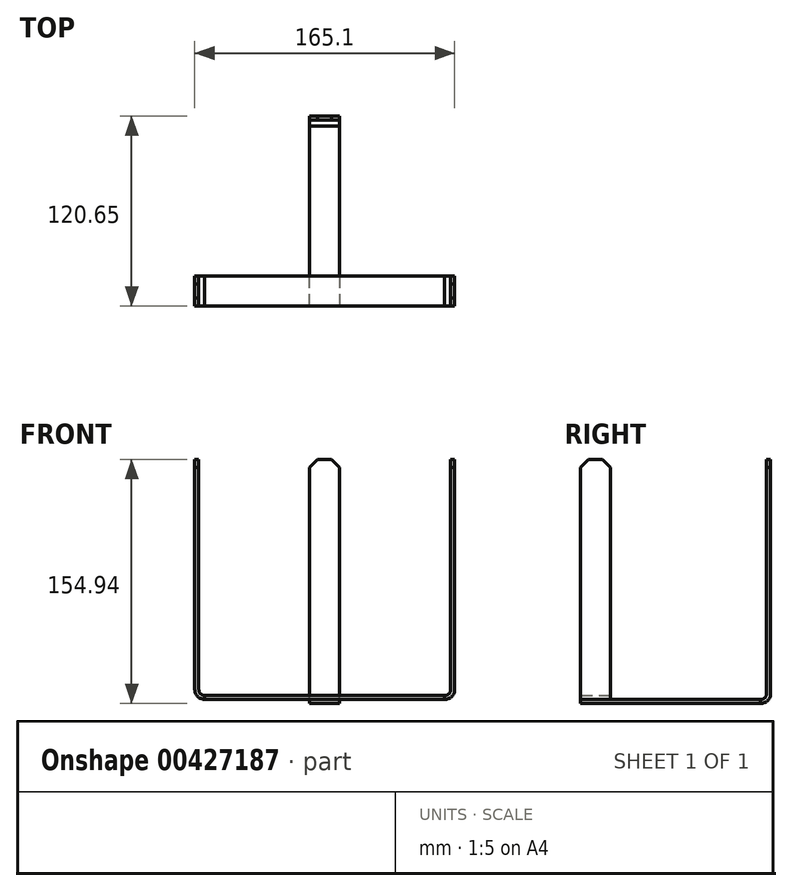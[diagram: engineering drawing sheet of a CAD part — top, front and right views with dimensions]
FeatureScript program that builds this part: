
annotation { "Feature Type Name" : "Feature", "Feature Type Description" : "" }
export const myFeature = defineFeature(function(context is Context, id is Id, definition is map)
    precondition{}
    {
        {
            var Q0;
            Q0=qCreatedBy(makeId("Top.planeOp"),FACE);
            var sketch = newSketch(context, id + "F0", { "sketchPlane" : qUnion([Q0])});
            skLineSegment(sketch, "E0.bottom", {"start": v(76.2, 9.53) * mm, "end": v(-76.2, 9.53) * mm});
            skLineSegment(sketch, "E0.top", {"start": v(76.2, -9.53) * mm, "end": v(-76.2, -9.53) * mm});
            skLineSegment(sketch, "E0.left", {"start": v(76.2, 9.53) * mm, "end": v(76.2, -9.53) * mm});
            skLineSegment(sketch, "E0.right", {"start": v(-76.2, 9.53) * mm, "end": v(-76.2, -9.53) * mm});
            skPoint(sketch, "E0.middle", {"position": v(0, 0) * mm});
            skLineSegment(sketch, "E1", {"start": v(0, 0) * mm, "end": v(-9.53, 0) * mm});
            skLineSegment(sketch, "E2", {"start": v(-9.53, -9.53) * mm, "end": v(-9.53, 104.78) * mm});
            skLineSegment(sketch, "E3", {"start": v(-9.53, 104.78) * mm, "end": v(9.52, 104.78) * mm});
            skLineSegment(sketch, "E4", {"start": v(9.52, 104.78) * mm, "end": v(9.53, -9.53) * mm});
            skSolve(sketch);
        }
        {
            var Q0;
            Q0=qCreatedBy(makeId("Front.planeOp"),FACE);
            var sketch = newSketch(context, id + "F1", { "sketchPlane" : qUnion([Q0])});
            skLineSegment(sketch, "E5", {"start": v(0, 0) * mm, "end": v(76.2, 0) * mm});
            skLineSegment(sketch, "E6", {"start": v(0, 0) * mm, "end": v(-76.2, 0) * mm});
            skArc(sketch, "E7", {"start": v(76.2, 0) * mm, "mid": v(80.7, 1.86) * mm, "end": v(82.55, 6.35) * mm});
            skArc(sketch, "E8", {"start": v(-82.55, 6.35) * mm, "mid": v(-80.7, 1.86) * mm, "end": v(-76.2, 0) * mm});
            skLineSegment(sketch, "E9", {"start": v(82.55, 0) * mm, "end": v(101.39, 0) * mm});
            skLineSegment(sketch, "E10", {"start": v(-82.55, 0) * mm, "end": v(-98.59, 0) * mm});
            skLineSegment(sketch, "E11", {"start": v(-82.55, 6.35) * mm, "end": v(-82.55, 21.04) * mm});
            skLineSegment(sketch, "E12", {"start": v(82.55, 6.35) * mm, "end": v(82.55, 20.48) * mm});
            skLineSegment(sketch, "E13", {"start": v(82.55, 6.35) * mm, "end": v(82.55, 152.4) * mm});
            skLineSegment(sketch, "E14", {"start": v(-82.55, 6.35) * mm, "end": v(-82.55, 152.4) * mm});
            skSolve(sketch);
        }
        {
            var Q0;
            Q0=qCreatedBy(makeId("Right.planeOp"),FACE);
            cPlane(context, id + "F2", {"entities" : qUnion([Q0]), "cplaneType" : CPlaneType.OFFSET, "offset" : 76.2 * mm, "width" : 152.4 * mm, "height" : 152.4 * mm});
        }
        {
            var Q0;
            Q0=qCreatedBy(id+"F2.planeOp",FACE);
            var sketch = newSketch(context, id + "F3", { "sketchPlane" : qUnion([Q0])});
            skLineSegment(sketch, "E15", {"start": v(0, 0) * mm, "end": v(-9.53, 0) * mm});
            skLineSegment(sketch, "E16", {"start": v(0, 0) * mm, "end": v(9.53, 0) * mm});
            skLineSegment(sketch, "E17", {"start": v(-9.53, 0) * mm, "end": v(-9.53, 2.54) * mm});
            skLineSegment(sketch, "E18", {"start": v(-9.53, 2.54) * mm, "end": v(9.53, 2.54) * mm});
            skLineSegment(sketch, "E19", {"start": v(9.53, 2.54) * mm, "end": v(9.53, 0) * mm});
            skSolve(sketch);
        }
        {
            var Q0;
            Q0=makeQuery(id+"F3.imprint","IMPRINT",FACE,{"disambiguationData":[TD([[makeQuery(id+"F3.imprint","IMPRINT",EDGE,{"derivedFrom":sQuery(id+"F3.wireOp",EDGE,"E15")}),-1.0]])]});
            var Q1;
            Q1=sQuery(id+"F1.wireOp",EDGE,"E13");
            var Q2;
            Q2=sQuery(id+"F1.wireOp",EDGE,"E7");
            sweep(context, id + "F4", {"profiles" : qUnion([Q0]), "path" : qUnion([Q1, Q2])});
        }
        {
            var Q0;
            Q0=qCreatedBy(makeId("Right.planeOp"),FACE);
            cPlane(context, id + "F5", {"entities" : qUnion([Q0]), "cplaneType" : CPlaneType.OFFSET, "offset" : 76.2 * mm, "oppositeDirection" : true, "width" : 152.4 * mm, "height" : 152.4 * mm});
        }
        {
            var Q0;
            Q0=qCreatedBy(id+"F5.planeOp",FACE);
            var sketch = newSketch(context, id + "F6", { "sketchPlane" : qUnion([Q0])});
            skLineSegment(sketch, "E20", {"start": v(0, 0) * mm, "end": v(-9.53, 0) * mm});
            skLineSegment(sketch, "E21", {"start": v(-9.53, 0) * mm, "end": v(-9.53, 2.54) * mm});
            skLineSegment(sketch, "E22", {"start": v(-9.53, 2.54) * mm, "end": v(9.53, 2.54) * mm});
            skLineSegment(sketch, "E23", {"start": v(9.53, 2.54) * mm, "end": v(9.53, 0) * mm});
            skLineSegment(sketch, "E24", {"start": v(9.53, 0) * mm, "end": v(0, 0) * mm});
            skSolve(sketch);
        }
        {
            var Q0;
            Q0=makeQuery(id+"F6.imprint","IMPRINT",FACE,{"disambiguationData":[TD([[makeQuery(id+"F6.imprint","IMPRINT",EDGE,{"derivedFrom":sQuery(id+"F6.wireOp",EDGE,"E20")}),-1.0]])]});
            var Q1;
            Q1=sQuery(id+"F1.wireOp",EDGE,"E8");
            var Q2;
            Q2=sQuery(id+"F1.wireOp",EDGE,"E14");
            sweep(context, id + "F7", {"profiles" : qUnion([Q0]), "path" : qUnion([Q1, Q2])});
        }
        {
            var Q0;
            {var subQ4=sQuery(id+"F0.wireOp",EDGE,"E0.right");Q0=makeQuery(id+"F0.imprint","IMPRINT",FACE,{"disambiguationData":[TD([[makeQuery(id+"F0.imprint","IMPRINT",EDGE,{"derivedFrom":subQ4}),1.0]])]});}
            var Q1;
            {var subQ0=sQuery(id+"F0.wireOp",EDGE,"E2");var subQ1=makeQuery(id+"F0.imprint","IMPRINT",VERTEX,{"derivedFrom":subQ0});Q1=makeQuery(id+"F0.imprint","IMPRINT",FACE,{"disambiguationData":[TD([[makeQuery(id+"F0.imprint","IMPRINT",EDGE,{"disambiguationData":[TD([[subQ1,1.0]])],"derivedFrom":subQ0}),-1.0]])]});}
            var Q2;
            {var subQ0=sQuery(id+"F0.wireOp",EDGE,"E0.left");Q2=makeQuery(id+"F0.imprint","IMPRINT",FACE,{"disambiguationData":[TD([[makeQuery(id+"F0.imprint","IMPRINT",EDGE,{"derivedFrom":subQ0}),-1.0]])]});}
            extrude(context, id + "F8", {"entities" : qUnion([Q0, Q1, Q2]), "depth" : 2.54 * mm});
        }
        {
            var Q0;
            Q0=qCreatedBy(makeId("Front.planeOp"),FACE);
            cPlane(context, id + "F9", {"entities" : qUnion([Q0]), "cplaneType" : CPlaneType.OFFSET, "offset" : 104.77 * mm, "oppositeDirection" : true, "width" : 152.4 * mm, "height" : 152.4 * mm});
        }
        {
            var Q0;
            Q0=qCreatedBy(id+"F9.planeOp",FACE);
            var sketch = newSketch(context, id + "F10", { "sketchPlane" : qUnion([Q0])});
            skLineSegment(sketch, "E25", {"start": v(0, 0) * mm, "end": v(9.53, 0) * mm});
            skLineSegment(sketch, "E26", {"start": v(9.53, 0) * mm, "end": v(9.53, 3.73) * mm});
            skLineSegment(sketch, "E27", {"start": v(9.53, 3.73) * mm, "end": v(-9.53, 3.73) * mm});
            skLineSegment(sketch, "E28", {"start": v(-9.53, 3.73) * mm, "end": v(-9.53, 0) * mm});
            skLineSegment(sketch, "E29", {"start": v(-9.53, 0) * mm, "end": v(0, 0) * mm});
            skLineSegment(sketch, "E30", {"start": v(9.53, 0) * mm, "end": v(9.53, -2.54) * mm});
            skLineSegment(sketch, "E31", {"start": v(9.53, -2.54) * mm, "end": v(-9.53, -2.54) * mm});
            skLineSegment(sketch, "E32", {"start": v(-9.53, -2.54) * mm, "end": v(-9.53, 0) * mm});
            skSolve(sketch);
        }
        {
            var Q0;
            Q0=qCreatedBy(makeId("Right.planeOp"),FACE);
            var sketch = newSketch(context, id + "F11", { "sketchPlane" : qUnion([Q0])});
            skLineSegment(sketch, "E33", {"start": v(0, 0) * mm, "end": v(0, -2.54) * mm});
            skLineSegment(sketch, "E34", {"start": v(0, -2.54) * mm, "end": v(104.78, -2.54) * mm});
            skArc(sketch, "E35", {"start": v(104.78, -2.54) * mm, "mid": v(109.27, -0.68) * mm, "end": v(111.12, 3.81) * mm});
            skLineSegment(sketch, "E36", {"start": v(111.13, 3.81) * mm, "end": v(111.13, 22.7) * mm});
            skLineSegment(sketch, "E37", {"start": v(111.13, 3.81) * mm, "end": v(111.13, 152.4) * mm});
            skSolve(sketch);
        }
        {
            var Q0;
            Q0=makeQuery(id+"F10.imprint","IMPRINT",FACE,{"disambiguationData":[TD([[makeQuery(id+"F10.imprint","IMPRINT",EDGE,{"derivedFrom":sQuery(id+"F10.wireOp",EDGE,"E25")}),-1.0]])]});
            var Q1;
            Q1=sQuery(id+"F11.wireOp",EDGE,"E35");
            var Q2;
            Q2=sQuery(id+"F11.wireOp",EDGE,"E37");
            sweep(context, id + "F12", {"profiles" : qUnion([Q0]), "path" : qUnion([Q1, Q2])});
        }
        {
            var Q0;
            {var subQ5=sQuery(id+"F0.wireOp",EDGE,"E3");Q0=makeQuery(id+"F0.imprint","IMPRINT",FACE,{"disambiguationData":[TD([[makeQuery(id+"F0.imprint","IMPRINT",EDGE,{"derivedFrom":subQ5}),-1.0]])]});}
            var Q1;
            {var subQ0=sQuery(id+"F0.wireOp",EDGE,"E2");var subQ1=makeQuery(id+"F0.imprint","IMPRINT",VERTEX,{"derivedFrom":subQ0});Q1=makeQuery(id+"F0.imprint","IMPRINT",FACE,{"disambiguationData":[TD([[makeQuery(id+"F0.imprint","IMPRINT",EDGE,{"disambiguationData":[TD([[subQ1,1.0]])],"derivedFrom":subQ0}),-1.0]])]});}
            extrude(context, id + "F13", {"entities" : qUnion([Q0, Q1]), "oppositeDirection" : true, "depth" : 2.54 * mm});
        }
        {
            var Q0;
            Q0=makeQuery(id+"F12.opSweep","CAP_EDGE",EDGE,{"disambiguationData":[OSD([sQuery(id+"F10.wireOp",EDGE,"E30"),sQuery(id+"F11.wireOp",VERTEX,"E37.end")])],"isStart":false});
            var Q1;
            Q1=makeQuery(id+"F12.opSweep","CAP_EDGE",EDGE,{"disambiguationData":[OSD([sQuery(id+"F10.wireOp",EDGE,"E32"),sQuery(id+"F11.wireOp",VERTEX,"E37.end")])],"isStart":false});
            var Q2;
            Q2=makeQuery(id+"F7.opSweep","CAP_EDGE",EDGE,{"disambiguationData":[OSD([sQuery(id+"F1.wireOp",VERTEX,"E14.end"),sQuery(id+"F6.wireOp",EDGE,"E21")])],"isStart":false});
            var Q3;
            Q3=makeQuery(id+"F7.opSweep","CAP_EDGE",EDGE,{"disambiguationData":[OSD([sQuery(id+"F1.wireOp",VERTEX,"E14.end"),sQuery(id+"F6.wireOp",EDGE,"E23")])],"isStart":false});
            var Q4;
            Q4=makeQuery(id+"F4.opSweep","CAP_EDGE",EDGE,{"disambiguationData":[OSD([sQuery(id+"F1.wireOp",VERTEX,"E13.end"),sQuery(id+"F3.wireOp",EDGE,"E17")])],"isStart":false});
            var Q5;
            Q5=makeQuery(id+"F4.opSweep","CAP_EDGE",EDGE,{"disambiguationData":[OSD([sQuery(id+"F1.wireOp",VERTEX,"E13.end"),sQuery(id+"F3.wireOp",EDGE,"E19")])],"isStart":false});
            chamfer(context, id + "F14", {"entities" : qUnion([Q0, Q1, Q2, Q3, Q4, Q5]), "width" : 5.08 * mm, "tangentPropagation" : true});
        }
    });
